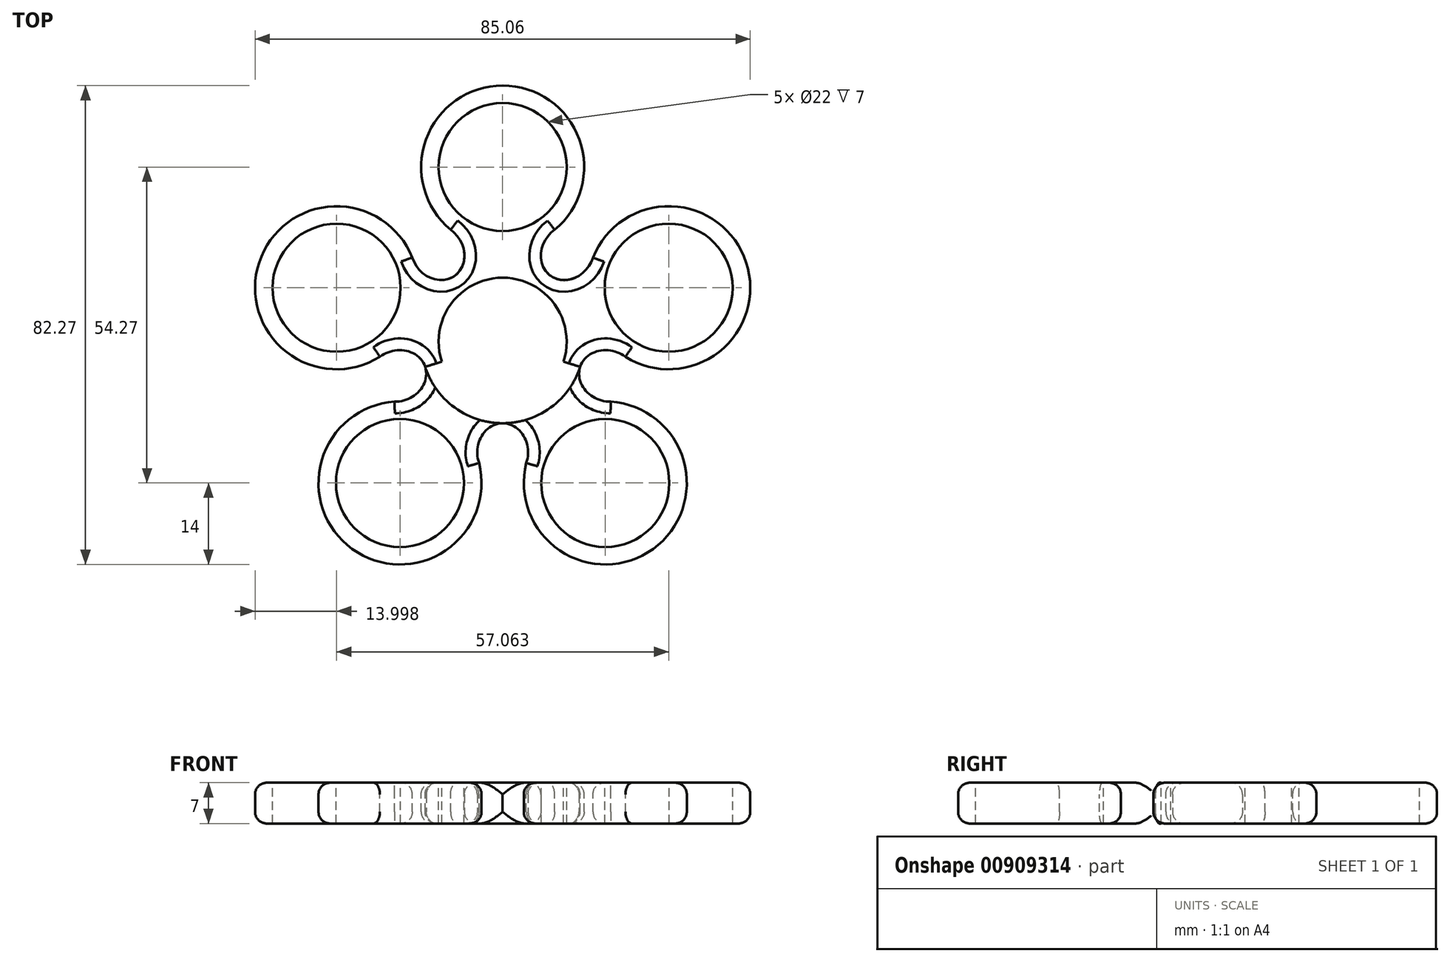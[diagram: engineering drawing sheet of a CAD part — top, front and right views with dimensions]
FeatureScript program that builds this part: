
annotation { "Feature Type Name" : "Feature", "Feature Type Description" : "" }
export const myFeature = defineFeature(function(context is Context, id is Id, definition is map)
    precondition{}
    {
        {
            var Q0;
            Q0=qCreatedBy(makeId("Top.planeOp"),FACE);
            var sketch = newSketch(context, id + "F0", { "sketchPlane" : qUnion([Q0])});
            skCircle(sketch, "E0", {"center": v(0, 0) * mm, "radius": 30 * mm});
            skCircle(sketch, "E1", {"center": v(0, 0) * mm, "radius": 44 * mm});
            skCircle(sketch, "E2.cCircle", {"center": v(0, 0) * mm, "radius": 44 * mm, "construction": true});
            skCircle(sketch, "E3.cCircle", {"center": v(0, 0) * mm, "radius": 30 * mm, "construction": true});
            skPoint(sketch, "E3.cCircle.perimeterSnap0", {"position": v(0, -19.5) * mm});
            skPoint(sketch, "E3.0.startSnap0", {"position": v(0, -24.5) * mm});
            skLineSegment(sketch, "E4", {"start": v(0, 44) * mm, "end": v(0, -30) * mm});
            skCircle(sketch, "E5", {"center": v(0, 30) * mm, "radius": 14 * mm});
            skCircle(sketch, "E6", {"center": v(0, 0) * mm, "radius": 11 * mm});
            skCircle(sketch, "E7", {"center": v(0, 30) * mm, "radius": 11 * mm});
            skPoint(sketch, "E8", {"position": v(29.84, 32.33) * mm});
            skLineSegment(sketch, "E9.0", {"start": v(0, 30) * mm, "end": v(28.53, 9.27) * mm});
            skLineSegment(sketch, "E9.1", {"start": v(28.53, 9.27) * mm, "end": v(17.63, -24.27) * mm});
            skLineSegment(sketch, "E9.2", {"start": v(17.63, -24.27) * mm, "end": v(-17.63, -24.27) * mm});
            skLineSegment(sketch, "E9.3", {"start": v(-17.63, -24.27) * mm, "end": v(-28.53, 9.27) * mm});
            skLineSegment(sketch, "E9.4", {"start": v(-28.53, 9.27) * mm, "end": v(0, 30) * mm});
            skCircle(sketch, "E10", {"center": v(28.53, 9.27) * mm, "radius": 14 * mm});
            skCircle(sketch, "E11", {"center": v(17.63, -24.27) * mm, "radius": 14 * mm});
            skCircle(sketch, "E12", {"center": v(-17.63, -24.27) * mm, "radius": 14 * mm});
            skCircle(sketch, "E13", {"center": v(-28.53, 9.27) * mm, "radius": 14 * mm});
            skCircle(sketch, "E14", {"center": v(-28.53, 9.27) * mm, "radius": 11 * mm});
            skCircle(sketch, "E15", {"center": v(-17.63, -24.27) * mm, "radius": 11 * mm});
            skCircle(sketch, "E16", {"center": v(17.63, -24.27) * mm, "radius": 11 * mm});
            skCircle(sketch, "E17", {"center": v(28.53, 9.27) * mm, "radius": 11 * mm});
            skCircle(sketch, "E18", {"center": v(0, 0) * mm, "radius": 14 * mm});
            skLineSegment(sketch, "E19", {"start": v(0, 0) * mm, "end": v(14.27, 19.64) * mm});
            skLineSegment(sketch, "E20", {"start": v(0, 0) * mm, "end": v(-14.27, 19.64) * mm});
            skLineSegment(sketch, "E21", {"start": v(0, 0) * mm, "end": v(-23.08, -7.5) * mm});
            skLineSegment(sketch, "E22", {"start": v(0, 0) * mm, "end": v(23.08, -7.5) * mm});
            skPoint(sketch, "E23", {"position": v(13.31, -4.33) * mm});
            skPoint(sketch, "E24", {"position": v(8.23, 11.33) * mm});
            skPoint(sketch, "E25", {"position": v(-8.23, 11.33) * mm});
            skPoint(sketch, "E26", {"position": v(-13.31, -4.33) * mm});
            skPoint(sketch, "E27", {"position": v(0, -14) * mm});
            skCircle(sketch, "E28", {"center": v(0, 0) * mm, "radius": 19 * mm});
            skEllipse(sketch, "E29", {"center": v(11.17, 15.37) * mm, "majorRadius": 5 * mm, "minorRadius": 4.36 * mm, "majorAxis": v(-0.59, -0.8)});
            skEllipse(sketch, "E30", {"center": v(-11.17, 15.37) * mm, "majorRadius": 5 * mm, "minorRadius": 4.36 * mm, "majorAxis": v(0.59, -0.8)});
            skEllipse(sketch, "E31", {"center": v(-18.07, -5.87) * mm, "majorRadius": 5 * mm, "minorRadius": 4.37 * mm, "majorAxis": v(0.95, 0.3)});
            skEllipse(sketch, "E32", {"center": v(0, -19) * mm, "majorRadius": 5 * mm, "minorRadius": 4.37 * mm, "majorAxis": v(0, 1)});
            skEllipse(sketch, "E33", {"center": v(18.07, -5.87) * mm, "majorRadius": 5 * mm, "minorRadius": 4.37 * mm, "majorAxis": v(-0.95, 0.3)});
            skSolve(sketch);
        }
        {
            var Q0;
            {var subQ0=sQuery(id+"F0.wireOp",EDGE,"rT3lhtyj-h4yS-NPWq-Tq2n-E2njMUcIvS19");var subQ1=sQuery(id+"F0.wireOp",EDGE,"E3.1");var subQ2=makeQuery(id+"F0.imprint","INTERSECT",VERTEX,{"derivedFrom":[subQ1,subQ0]});Q0=makeQuery(id+"F0.imprint","IMPRINT",FACE,{"disambiguationData":[TD([[makeQuery(id+"F0.imprint","IMPRINT",EDGE,{"disambiguationData":[TD([[subQ2,-1.0]])],"derivedFrom":subQ1}),1.0]])]});}
            var Q1;
            {var subQ0=sQuery(id+"F0.wireOp",EDGE,"E5");var subQ1=sQuery(id+"F0.wireOp",EDGE,"E3.1");var subQ2=makeQuery(id+"F0.imprint","INTERSECT",VERTEX,{"disambiguationData":[OD(1.0)],"derivedFrom":[subQ1,subQ0]});Q1=makeQuery(id+"F0.imprint","IMPRINT",FACE,{"disambiguationData":[TD([[makeQuery(id+"F0.imprint","IMPRINT",EDGE,{"disambiguationData":[TD([[subQ2,-1.0]])],"derivedFrom":subQ1}),1.0]])]});}
            var Q2;
            {var subQ0=sQuery(id+"F0.wireOp",EDGE,"E5");var subQ1=sQuery(id+"F0.wireOp",EDGE,"E0");var subQ2=makeQuery(id+"F0.imprint","INTERSECT",VERTEX,{"disambiguationData":[OD(0.0)],"derivedFrom":[subQ1,subQ0]});Q2=makeQuery(id+"F0.imprint","IMPRINT",FACE,{"disambiguationData":[TD([[makeQuery(id+"F0.imprint","IMPRINT",EDGE,{"disambiguationData":[TD([[subQ2,-1.0]])],"derivedFrom":subQ1}),-1.0]])]});}
            var Q3;
            {var subQ0=sQuery(id+"F0.wireOp",EDGE,"dxAisywA-VBGr-Pawd-wR7n-FkVNZc5FjTRd");var subQ1=sQuery(id+"F0.wireOp",EDGE,"E0");var subQ2=makeQuery(id+"F0.imprint","INTERSECT",VERTEX,{"disambiguationData":[OD(1.0)],"derivedFrom":[subQ1,subQ0]});Q3=makeQuery(id+"F0.imprint","IMPRINT",FACE,{"disambiguationData":[TD([[makeQuery(id+"F0.imprint","IMPRINT",EDGE,{"disambiguationData":[TD([[subQ2,-1.0]])],"derivedFrom":subQ1}),1.0]])]});}
            var Q4;
            {var subQ0=sQuery(id+"F0.wireOp",EDGE,"dxAisywA-VBGr-Pawd-wR7n-FkVNZc5FjTRd");var subQ1=sQuery(id+"F0.wireOp",EDGE,"E0");var subQ2=makeQuery(id+"F0.imprint","INTERSECT",VERTEX,{"disambiguationData":[OD(1.0)],"derivedFrom":[subQ1,subQ0]});Q4=makeQuery(id+"F0.imprint","IMPRINT",FACE,{"disambiguationData":[TD([[makeQuery(id+"F0.imprint","IMPRINT",EDGE,{"disambiguationData":[TD([[subQ2,-1.0]])],"derivedFrom":subQ1}),-1.0]])]});}
            var Q5;
            {var subQ0=sQuery(id+"F0.wireOp",EDGE,"dxAisywA-VBGr-Pawd-wR7n-FkVNZc5FjTRd");var subQ1=sQuery(id+"F0.wireOp",EDGE,"E0");var subQ2=makeQuery(id+"F0.imprint","INTERSECT",VERTEX,{"disambiguationData":[OD(0.0)],"derivedFrom":[subQ1,subQ0]});Q5=makeQuery(id+"F0.imprint","IMPRINT",FACE,{"disambiguationData":[TD([[makeQuery(id+"F0.imprint","IMPRINT",EDGE,{"disambiguationData":[TD([[subQ2,1.0]])],"derivedFrom":subQ1}),-1.0]])]});}
            var Q6;
            {var subQ0=sQuery(id+"F0.wireOp",EDGE,"RqG3pEgj-UPx2-bqY4-tycd-a4pZXK4rwrWL");var subQ1=sQuery(id+"F0.wireOp",EDGE,"E0");var subQ2=makeQuery(id+"F0.imprint","INTERSECT",VERTEX,{"disambiguationData":[OD(0.0)],"derivedFrom":[subQ1,subQ0]});Q6=makeQuery(id+"F0.imprint","IMPRINT",FACE,{"disambiguationData":[TD([[makeQuery(id+"F0.imprint","IMPRINT",EDGE,{"disambiguationData":[TD([[subQ2,-1.0]])],"derivedFrom":subQ1}),-1.0]])]});}
            var Q7;
            {var subQ0=sQuery(id+"F0.wireOp",EDGE,"RqG3pEgj-UPx2-bqY4-tycd-a4pZXK4rwrWL");var subQ1=sQuery(id+"F0.wireOp",EDGE,"E3.0");var subQ2=makeQuery(id+"F0.imprint","INTERSECT",VERTEX,{"disambiguationData":[OD(0.0)],"derivedFrom":[subQ1,subQ0]});Q7=makeQuery(id+"F0.imprint","IMPRINT",FACE,{"disambiguationData":[TD([[makeQuery(id+"F0.imprint","IMPRINT",EDGE,{"disambiguationData":[TD([[subQ2,-1.0]])],"derivedFrom":subQ1}),-1.0]])]});}
            var Q8;
            {var subQ0=sQuery(id+"F0.wireOp",EDGE,"0NMUeHQV-vgPk-UNAw-vjHk-L7wlCvfe4npe");var subQ1=sQuery(id+"F0.wireOp",EDGE,"E3.0");var subQ2=makeQuery(id+"F0.imprint","INTERSECT",VERTEX,{"derivedFrom":[subQ1,subQ0]});Q8=makeQuery(id+"F0.imprint","IMPRINT",FACE,{"disambiguationData":[TD([[makeQuery(id+"F0.imprint","IMPRINT",EDGE,{"disambiguationData":[TD([[subQ2,-1.0]])],"derivedFrom":subQ1}),-1.0]])]});}
            var Q9;
            {var subQ0=sQuery(id+"F0.wireOp",EDGE,"E5");var subQ1=sQuery(id+"F0.wireOp",EDGE,"E3.1");var subQ2=makeQuery(id+"F0.imprint","INTERSECT",VERTEX,{"disambiguationData":[OD(0.0)],"derivedFrom":[subQ1,subQ0]});Q9=makeQuery(id+"F0.imprint","IMPRINT",FACE,{"disambiguationData":[TD([[makeQuery(id+"F0.imprint","IMPRINT",EDGE,{"disambiguationData":[TD([[subQ2,-1.0]])],"derivedFrom":subQ1}),-1.0]])]});}
            var Q10;
            {var subQ0=sQuery(id+"F0.wireOp",EDGE,"dxAisywA-VBGr-Pawd-wR7n-FkVNZc5FjTRd");var subQ1=sQuery(id+"F0.wireOp",EDGE,"E3.2");var subQ2=makeQuery(id+"F0.imprint","INTERSECT",VERTEX,{"disambiguationData":[OD(0.0)],"derivedFrom":[subQ1,subQ0]});Q10=makeQuery(id+"F0.imprint","IMPRINT",FACE,{"disambiguationData":[TD([[makeQuery(id+"F0.imprint","IMPRINT",EDGE,{"disambiguationData":[TD([[subQ2,-1.0]])],"derivedFrom":subQ1}),-1.0]])]});}
            var Q11;
            {var subQ0=sQuery(id+"F0.wireOp",EDGE,"QKBKVQNg-VhWM-ZNxB-FvfL-6iABSSp7N5gX");var subQ1=sQuery(id+"F0.wireOp",EDGE,"E3.2");var subQ2=makeQuery(id+"F0.imprint","INTERSECT",VERTEX,{"derivedFrom":[subQ1,subQ0]});Q11=makeQuery(id+"F0.imprint","IMPRINT",FACE,{"disambiguationData":[TD([[makeQuery(id+"F0.imprint","IMPRINT",EDGE,{"disambiguationData":[TD([[subQ2,-1.0]])],"derivedFrom":subQ1}),-1.0]])]});}
            var Q12;
            {var subQ0=sQuery(id+"F0.wireOp",EDGE,"E5");var subQ1=sQuery(id+"F0.wireOp",EDGE,"E0");var subQ2=makeQuery(id+"F0.imprint","INTERSECT",VERTEX,{"disambiguationData":[OD(0.0)],"derivedFrom":[subQ1,subQ0]});Q12=makeQuery(id+"F0.imprint","IMPRINT",FACE,{"disambiguationData":[TD([[makeQuery(id+"F0.imprint","IMPRINT",EDGE,{"disambiguationData":[TD([[subQ2,-1.0]])],"derivedFrom":subQ1}),1.0]])]});}
            var Q13;
            {var subQ0=sQuery(id+"F0.wireOp",EDGE,"dxAisywA-VBGr-Pawd-wR7n-FkVNZc5FjTRd");var subQ1=sQuery(id+"F0.wireOp",EDGE,"E0");var subQ2=makeQuery(id+"F0.imprint","INTERSECT",VERTEX,{"disambiguationData":[OD(0.0)],"derivedFrom":[subQ1,subQ0]});Q13=makeQuery(id+"F0.imprint","IMPRINT",FACE,{"disambiguationData":[TD([[makeQuery(id+"F0.imprint","IMPRINT",EDGE,{"disambiguationData":[TD([[subQ2,1.0]])],"derivedFrom":subQ1}),1.0]])]});}
            var Q14;
            {var subQ0=sQuery(id+"F0.wireOp",EDGE,"RqG3pEgj-UPx2-bqY4-tycd-a4pZXK4rwrWL");var subQ1=sQuery(id+"F0.wireOp",EDGE,"E0");var subQ2=makeQuery(id+"F0.imprint","INTERSECT",VERTEX,{"disambiguationData":[OD(0.0)],"derivedFrom":[subQ1,subQ0]});Q14=makeQuery(id+"F0.imprint","IMPRINT",FACE,{"disambiguationData":[TD([[makeQuery(id+"F0.imprint","IMPRINT",EDGE,{"disambiguationData":[TD([[subQ2,-1.0]])],"derivedFrom":subQ1}),1.0]])]});}
            var Q15;
            {var subQ0=sQuery(id+"F0.wireOp",EDGE,"E4");var subQ1=sQuery(id+"F0.wireOp",EDGE,"E3.1");var subQ2=makeQuery(id+"F0.imprint","INTERSECT",VERTEX,{"derivedFrom":[subQ1,subQ0]});Q15=makeQuery(id+"F0.imprint","IMPRINT",FACE,{"disambiguationData":[TD([[makeQuery(id+"F0.imprint","IMPRINT",EDGE,{"disambiguationData":[TD([[subQ2,-1.0]])],"derivedFrom":subQ1}),-1.0]])]});}
            var Q16;
            {var subQ1=sQuery(id+"F0.wireOp",EDGE,"E3.1");var subQ5=sQuery(id+"F0.wireOp",EDGE,"E5");var subQ6=makeQuery(id+"F0.imprint","INTERSECT",VERTEX,{"disambiguationData":[OD(1.0)],"derivedFrom":[subQ1,subQ5]});Q16=makeQuery(id+"F0.imprint","IMPRINT",FACE,{"disambiguationData":[TD([[makeQuery(id+"F0.imprint","IMPRINT",EDGE,{"disambiguationData":[TD([[subQ6,-1.0]])],"derivedFrom":subQ1}),-1.0]])]});}
            var Q17;
            {var subQ1=sQuery(id+"F0.wireOp",EDGE,"E3.2");var subQ5=sQuery(id+"F0.wireOp",EDGE,"sHA2WUK1-COiN-vLBo-81U8-SncWV65uhgPs");var subQ9=makeQuery(id+"F0.imprint","INTERSECT",VERTEX,{"derivedFrom":[subQ1,subQ5]});Q17=makeQuery(id+"F0.imprint","IMPRINT",FACE,{"disambiguationData":[TD([[makeQuery(id+"F0.imprint","IMPRINT",EDGE,{"disambiguationData":[TD([[subQ9,-1.0]])],"derivedFrom":subQ1}),-1.0]])]});}
            var Q18;
            {var subQ1=sQuery(id+"F0.wireOp",EDGE,"E3.0");var subQ5=sQuery(id+"F0.wireOp",EDGE,"RqG3pEgj-UPx2-bqY4-tycd-a4pZXK4rwrWL");var subQ6=makeQuery(id+"F0.imprint","INTERSECT",VERTEX,{"disambiguationData":[OD(1.0)],"derivedFrom":[subQ1,subQ5]});Q18=makeQuery(id+"F0.imprint","IMPRINT",FACE,{"disambiguationData":[TD([[makeQuery(id+"F0.imprint","IMPRINT",EDGE,{"disambiguationData":[TD([[subQ6,-1.0]])],"derivedFrom":subQ1}),-1.0]])]});}
            var Q19;
            {var subQ1=sQuery(id+"F0.wireOp",EDGE,"E3.0");var subQ7=sQuery(id+"F0.wireOp",EDGE,"ZJlmTgZx-EINA-FnJ0-EF4e-C9FzmJizpjkO");var subQ9=makeQuery(id+"F0.imprint","INTERSECT",VERTEX,{"derivedFrom":[subQ1,subQ7]});Q19=makeQuery(id+"F0.imprint","IMPRINT",FACE,{"disambiguationData":[TD([[makeQuery(id+"F0.imprint","IMPRINT",EDGE,{"disambiguationData":[TD([[subQ9,-1.0]])],"derivedFrom":subQ1}),-1.0]])]});}
            var Q20;
            {var subQ1=sQuery(id+"F0.wireOp",EDGE,"E3.2");var subQ7=sQuery(id+"F0.wireOp",EDGE,"dxAisywA-VBGr-Pawd-wR7n-FkVNZc5FjTRd");var subQ8=makeQuery(id+"F0.imprint","INTERSECT",VERTEX,{"disambiguationData":[OD(1.0)],"derivedFrom":[subQ1,subQ7]});Q20=makeQuery(id+"F0.imprint","IMPRINT",FACE,{"disambiguationData":[TD([[makeQuery(id+"F0.imprint","IMPRINT",EDGE,{"disambiguationData":[TD([[subQ8,-1.0]])],"derivedFrom":subQ1}),-1.0]])]});}
            var Q21;
            {var subQ0=sQuery(id+"F0.wireOp",EDGE,"RqG3pEgj-UPx2-bqY4-tycd-a4pZXK4rwrWL");var subQ1=sQuery(id+"F0.wireOp",EDGE,"E3.0");var subQ2=makeQuery(id+"F0.imprint","INTERSECT",VERTEX,{"disambiguationData":[OD(1.0)],"derivedFrom":[subQ1,subQ0]});Q21=makeQuery(id+"F0.imprint","IMPRINT",FACE,{"disambiguationData":[TD([[makeQuery(id+"F0.imprint","IMPRINT",EDGE,{"disambiguationData":[TD([[subQ2,-1.0]])],"derivedFrom":subQ1}),1.0]])]});}
            var Q22;
            {var subQ0=sQuery(id+"F0.wireOp",EDGE,"sHA2WUK1-COiN-vLBo-81U8-SncWV65uhgPs");var subQ1=sQuery(id+"F0.wireOp",EDGE,"E3.2");var subQ2=makeQuery(id+"F0.imprint","INTERSECT",VERTEX,{"derivedFrom":[subQ1,subQ0]});Q22=makeQuery(id+"F0.imprint","IMPRINT",FACE,{"disambiguationData":[TD([[makeQuery(id+"F0.imprint","IMPRINT",EDGE,{"disambiguationData":[TD([[subQ2,-1.0]])],"derivedFrom":subQ1}),1.0]])]});}
            var Q23;
            {var subQ0=sQuery(id+"F0.wireOp",EDGE,"ZJlmTgZx-EINA-FnJ0-EF4e-C9FzmJizpjkO");var subQ1=sQuery(id+"F0.wireOp",EDGE,"E3.0");var subQ2=makeQuery(id+"F0.imprint","INTERSECT",VERTEX,{"derivedFrom":[subQ1,subQ0]});Q23=makeQuery(id+"F0.imprint","IMPRINT",FACE,{"disambiguationData":[TD([[makeQuery(id+"F0.imprint","IMPRINT",EDGE,{"disambiguationData":[TD([[subQ2,-1.0]])],"derivedFrom":subQ1}),1.0]])]});}
            var Q24;
            {var subQ0=sQuery(id+"F0.wireOp",EDGE,"dxAisywA-VBGr-Pawd-wR7n-FkVNZc5FjTRd");var subQ1=sQuery(id+"F0.wireOp",EDGE,"E3.2");var subQ2=makeQuery(id+"F0.imprint","INTERSECT",VERTEX,{"disambiguationData":[OD(1.0)],"derivedFrom":[subQ1,subQ0]});Q24=makeQuery(id+"F0.imprint","IMPRINT",FACE,{"disambiguationData":[TD([[makeQuery(id+"F0.imprint","IMPRINT",EDGE,{"disambiguationData":[TD([[subQ2,-1.0]])],"derivedFrom":subQ1}),1.0]])]});}
            var Q25;
            {var subQ0=sQuery(id+"F0.wireOp",EDGE,"rT3lhtyj-h4yS-NPWq-Tq2n-E2njMUcIvS19");var subQ1=sQuery(id+"F0.wireOp",EDGE,"E3.1");var subQ2=makeQuery(id+"F0.imprint","INTERSECT",VERTEX,{"derivedFrom":[subQ1,subQ0]});Q25=makeQuery(id+"F0.imprint","IMPRINT",FACE,{"disambiguationData":[TD([[makeQuery(id+"F0.imprint","IMPRINT",EDGE,{"disambiguationData":[TD([[subQ2,-1.0]])],"derivedFrom":subQ1}),-1.0]])]});}
            var Q26;
            {var subQ1=sQuery(id+"F0.wireOp",EDGE,"E2.1");var subQ3=sQuery(id+"F0.wireOp",EDGE,"pn2p9FIU-HhLt-bJUs-He3U-jyiwcetz7rk5");var subQ4=makeQuery(id+"F0.imprint","INTERSECT",VERTEX,{"disambiguationData":[OD(1.0)],"derivedFrom":[subQ1,subQ3]});Q26=makeQuery(id+"F0.imprint","IMPRINT",FACE,{"disambiguationData":[TD([[makeQuery(id+"F0.imprint","IMPRINT",EDGE,{"disambiguationData":[TD([[subQ4,1.0]])],"derivedFrom":subQ3}),-1.0]])]});}
            var Q27;
            {var subQ0=sQuery(id+"F0.wireOp",EDGE,"pn2p9FIU-HhLt-bJUs-He3U-jyiwcetz7rk5");var subQ1=sQuery(id+"F0.wireOp",EDGE,"E0");var subQ2=makeQuery(id+"F0.imprint","INTERSECT",VERTEX,{"disambiguationData":[OD(1.0)],"derivedFrom":[subQ1,subQ0]});Q27=makeQuery(id+"F0.imprint","IMPRINT",FACE,{"disambiguationData":[TD([[makeQuery(id+"F0.imprint","IMPRINT",EDGE,{"disambiguationData":[TD([[subQ2,-1.0]])],"derivedFrom":subQ1}),-1.0]])]});}
            var Q28;
            {var subQ0=sQuery(id+"F0.wireOp",EDGE,"pn2p9FIU-HhLt-bJUs-He3U-jyiwcetz7rk5");var subQ1=sQuery(id+"F0.wireOp",EDGE,"E0");var subQ2=makeQuery(id+"F0.imprint","INTERSECT",VERTEX,{"disambiguationData":[OD(1.0)],"derivedFrom":[subQ1,subQ0]});Q28=makeQuery(id+"F0.imprint","IMPRINT",FACE,{"disambiguationData":[TD([[makeQuery(id+"F0.imprint","IMPRINT",EDGE,{"disambiguationData":[TD([[subQ2,-1.0]])],"derivedFrom":subQ1}),1.0]])]});}
            var Q29;
            {var subQ0=sQuery(id+"F0.wireOp",EDGE,"RqG3pEgj-UPx2-bqY4-tycd-a4pZXK4rwrWL");var subQ1=sQuery(id+"F0.wireOp",EDGE,"E3.0");var subQ2=makeQuery(id+"F0.imprint","INTERSECT",VERTEX,{"disambiguationData":[OD(0.0)],"derivedFrom":[subQ1,subQ0]});Q29=makeQuery(id+"F0.imprint","IMPRINT",FACE,{"disambiguationData":[TD([[makeQuery(id+"F0.imprint","IMPRINT",EDGE,{"disambiguationData":[TD([[subQ2,-1.0]])],"derivedFrom":subQ1}),1.0]])]});}
            var Q30;
            {var subQ1=sQuery(id+"F0.wireOp",EDGE,"E2.2");var subQ3=sQuery(id+"F0.wireOp",EDGE,"pn2p9FIU-HhLt-bJUs-He3U-jyiwcetz7rk5");var subQ4=makeQuery(id+"F0.imprint","INTERSECT",VERTEX,{"disambiguationData":[OD(0.0)],"derivedFrom":[subQ1,subQ3]});Q30=makeQuery(id+"F0.imprint","IMPRINT",FACE,{"disambiguationData":[TD([[makeQuery(id+"F0.imprint","IMPRINT",EDGE,{"disambiguationData":[TD([[subQ4,-1.0]])],"derivedFrom":subQ3}),-1.0]])]});}
            var Q31;
            {var subQ1=sQuery(id+"F0.wireOp",EDGE,"E3.0");var subQ5=sQuery(id+"F0.wireOp",EDGE,"0NMUeHQV-vgPk-UNAw-vjHk-L7wlCvfe4npe");var subQ6=makeQuery(id+"F0.imprint","INTERSECT",VERTEX,{"derivedFrom":[subQ1,subQ5]});Q31=makeQuery(id+"F0.imprint","IMPRINT",FACE,{"disambiguationData":[TD([[makeQuery(id+"F0.imprint","IMPRINT",EDGE,{"disambiguationData":[TD([[subQ6,-1.0]])],"derivedFrom":subQ1}),1.0]])]});}
            var Q32;
            {var subQ1=sQuery(id+"F0.wireOp",EDGE,"E3.2");var subQ5=sQuery(id+"F0.wireOp",EDGE,"QKBKVQNg-VhWM-ZNxB-FvfL-6iABSSp7N5gX");var subQ6=makeQuery(id+"F0.imprint","INTERSECT",VERTEX,{"derivedFrom":[subQ1,subQ5]});Q32=makeQuery(id+"F0.imprint","IMPRINT",FACE,{"disambiguationData":[TD([[makeQuery(id+"F0.imprint","IMPRINT",EDGE,{"disambiguationData":[TD([[subQ6,-1.0]])],"derivedFrom":subQ1}),1.0]])]});}
            var Q33;
            {var subQ1=sQuery(id+"F0.wireOp",EDGE,"E3.2");var subQ7=sQuery(id+"F0.wireOp",EDGE,"dxAisywA-VBGr-Pawd-wR7n-FkVNZc5FjTRd");var subQ9=makeQuery(id+"F0.imprint","INTERSECT",VERTEX,{"disambiguationData":[OD(0.0)],"derivedFrom":[subQ1,subQ7]});Q33=makeQuery(id+"F0.imprint","IMPRINT",FACE,{"disambiguationData":[TD([[makeQuery(id+"F0.imprint","IMPRINT",EDGE,{"disambiguationData":[TD([[subQ9,-1.0]])],"derivedFrom":subQ1}),1.0]])]});}
            var Q34;
            {var subQ1=sQuery(id+"F0.wireOp",EDGE,"E2.1");var subQ3=sQuery(id+"F0.wireOp",EDGE,"wBWbJlWF-WJeb-dRll-Lu5Z-CJGq9FSQDJmP");var subQ4=makeQuery(id+"F0.imprint","INTERSECT",VERTEX,{"disambiguationData":[OD(0.0)],"derivedFrom":[subQ1,subQ3]});Q34=makeQuery(id+"F0.imprint","IMPRINT",FACE,{"disambiguationData":[TD([[makeQuery(id+"F0.imprint","IMPRINT",EDGE,{"disambiguationData":[TD([[subQ4,-1.0]])],"derivedFrom":subQ3}),-1.0]])]});}
            var Q35;
            {var subQ1=sQuery(id+"F0.wireOp",EDGE,"E2.0");var subQ3=sQuery(id+"F0.wireOp",EDGE,"wBWbJlWF-WJeb-dRll-Lu5Z-CJGq9FSQDJmP");var subQ4=makeQuery(id+"F0.imprint","INTERSECT",VERTEX,{"disambiguationData":[OD(1.0)],"derivedFrom":[subQ1,subQ3]});Q35=makeQuery(id+"F0.imprint","IMPRINT",FACE,{"disambiguationData":[TD([[makeQuery(id+"F0.imprint","IMPRINT",EDGE,{"disambiguationData":[TD([[subQ4,1.0]])],"derivedFrom":subQ3}),-1.0]])]});}
            var Q36;
            {var subQ1=sQuery(id+"F0.wireOp",EDGE,"E3.1");var subQ5=sQuery(id+"F0.wireOp",EDGE,"E4");var subQ6=makeQuery(id+"F0.imprint","INTERSECT",VERTEX,{"derivedFrom":[subQ1,subQ5]});Q36=makeQuery(id+"F0.imprint","IMPRINT",FACE,{"disambiguationData":[TD([[makeQuery(id+"F0.imprint","IMPRINT",EDGE,{"disambiguationData":[TD([[subQ6,-1.0]])],"derivedFrom":subQ1}),1.0]])]});}
            var Q37;
            {var subQ1=sQuery(id+"F0.wireOp",EDGE,"E3.1");var subQ5=sQuery(id+"F0.wireOp",EDGE,"E5");var subQ6=makeQuery(id+"F0.imprint","INTERSECT",VERTEX,{"disambiguationData":[OD(0.0)],"derivedFrom":[subQ1,subQ5]});Q37=makeQuery(id+"F0.imprint","IMPRINT",FACE,{"disambiguationData":[TD([[makeQuery(id+"F0.imprint","IMPRINT",EDGE,{"disambiguationData":[TD([[subQ6,-1.0]])],"derivedFrom":subQ1}),1.0]])]});}
            var Q38;
            {var subQ0=sQuery(id+"F0.wireOp",EDGE,"E7");var subQ1=sQuery(id+"F0.wireOp",EDGE,"E0");var subQ2=makeQuery(id+"F0.imprint","INTERSECT",VERTEX,{"disambiguationData":[OD(1.0)],"derivedFrom":[subQ1,subQ0]});Q38=makeQuery(id+"F0.imprint","IMPRINT",FACE,{"disambiguationData":[TD([[makeQuery(id+"F0.imprint","IMPRINT",EDGE,{"disambiguationData":[TD([[subQ2,-1.0]])],"derivedFrom":subQ1}),-1.0]])]});}
            var Q39;
            {var subQ0=sQuery(id+"F0.wireOp",EDGE,"E7");var subQ1=sQuery(id+"F0.wireOp",EDGE,"E0");var subQ2=makeQuery(id+"F0.imprint","INTERSECT",VERTEX,{"disambiguationData":[OD(1.0)],"derivedFrom":[subQ1,subQ0]});Q39=makeQuery(id+"F0.imprint","IMPRINT",FACE,{"disambiguationData":[TD([[makeQuery(id+"F0.imprint","IMPRINT",EDGE,{"disambiguationData":[TD([[subQ2,-1.0]])],"derivedFrom":subQ1}),1.0]])]});}
            var Q40;
            {var subQ1=sQuery(id+"F0.wireOp",EDGE,"E2.0");var subQ3=sQuery(id+"F0.wireOp",EDGE,"E7");var subQ4=makeQuery(id+"F0.imprint","INTERSECT",VERTEX,{"disambiguationData":[OD(0.0)],"derivedFrom":[subQ1,subQ3]});Q40=makeQuery(id+"F0.imprint","IMPRINT",FACE,{"disambiguationData":[TD([[makeQuery(id+"F0.imprint","IMPRINT",EDGE,{"disambiguationData":[TD([[subQ4,-1.0]])],"derivedFrom":subQ3}),-1.0]])]});}
            var Q41;
            {var subQ1=sQuery(id+"F0.wireOp",EDGE,"E2.2");var subQ3=sQuery(id+"F0.wireOp",EDGE,"E7");var subQ4=makeQuery(id+"F0.imprint","INTERSECT",VERTEX,{"disambiguationData":[OD(1.0)],"derivedFrom":[subQ1,subQ3]});Q41=makeQuery(id+"F0.imprint","IMPRINT",FACE,{"disambiguationData":[TD([[makeQuery(id+"F0.imprint","IMPRINT",EDGE,{"disambiguationData":[TD([[subQ4,1.0]])],"derivedFrom":subQ3}),-1.0]])]});}
            var Q42;
            {var subQ1=sQuery(id+"F0.wireOp",EDGE,"E5");var subQ8=sQuery(id+"F0.wireOp",EDGE,"E28");var subQ10=makeQuery(id+"F0.imprint","INTERSECT",VERTEX,{"disambiguationData":[OD(1.0)],"derivedFrom":[subQ1,subQ8]});Q42=makeQuery(id+"F0.imprint","IMPRINT",FACE,{"disambiguationData":[TD([[makeQuery(id+"F0.imprint","IMPRINT",EDGE,{"disambiguationData":[TD([[subQ10,-1.0]])],"derivedFrom":subQ1}),1.0]])]});}
            var Q43;
            {var subQ0=sQuery(id+"F0.wireOp",EDGE,"E5");var subQ1=sQuery(id+"F0.wireOp",EDGE,"E4");var subQ2=makeQuery(id+"F0.imprint","INTERSECT",VERTEX,{"derivedFrom":[subQ1,subQ0]});Q43=makeQuery(id+"F0.imprint","IMPRINT",FACE,{"disambiguationData":[TD([[makeQuery(id+"F0.imprint","IMPRINT",EDGE,{"disambiguationData":[TD([[subQ2,-1.0]])],"derivedFrom":subQ0}),1.0]])]});}
            var Q44;
            {var subQ0=sQuery(id+"F0.wireOp",EDGE,"E5");var subQ1=sQuery(id+"F0.wireOp",EDGE,"E4");var subQ2=makeQuery(id+"F0.imprint","INTERSECT",VERTEX,{"derivedFrom":[subQ1,subQ0]});Q44=makeQuery(id+"F0.imprint","IMPRINT",FACE,{"disambiguationData":[TD([[makeQuery(id+"F0.imprint","IMPRINT",EDGE,{"disambiguationData":[TD([[subQ2,1.0]])],"derivedFrom":subQ0}),1.0]])]});}
            var Q45;
            {var subQ0=sQuery(id+"F0.wireOp",EDGE,"E9.4");var subQ6=sQuery(id+"F0.wireOp",EDGE,"E5");var subQ9=makeQuery(id+"F0.imprint","INTERSECT",VERTEX,{"derivedFrom":[subQ6,subQ0]});Q45=makeQuery(id+"F0.imprint","IMPRINT",FACE,{"disambiguationData":[TD([[makeQuery(id+"F0.imprint","IMPRINT",EDGE,{"disambiguationData":[TD([[subQ9,-1.0]])],"derivedFrom":subQ6}),1.0]])]});}
            var Q46;
            {var subQ2=sQuery(id+"F0.wireOp",EDGE,"E0");var subQ5=sQuery(id+"F0.wireOp",EDGE,"E17");var subQ7=makeQuery(id+"F0.imprint","INTERSECT",VERTEX,{"disambiguationData":[OD(0.0)],"derivedFrom":[subQ2,subQ5]});Q46=makeQuery(id+"F0.imprint","IMPRINT",FACE,{"disambiguationData":[TD([[makeQuery(id+"F0.imprint","IMPRINT",EDGE,{"disambiguationData":[TD([[subQ7,-1.0]])],"derivedFrom":subQ2}),-1.0]])]});}
            var Q47;
            {var subQ0=sQuery(id+"F0.wireOp",EDGE,"E17");var subQ1=sQuery(id+"F0.wireOp",EDGE,"E0");var subQ2=makeQuery(id+"F0.imprint","INTERSECT",VERTEX,{"disambiguationData":[OD(0.0)],"derivedFrom":[subQ1,subQ0]});Q47=makeQuery(id+"F0.imprint","IMPRINT",FACE,{"disambiguationData":[TD([[makeQuery(id+"F0.imprint","IMPRINT",EDGE,{"disambiguationData":[TD([[subQ2,-1.0]])],"derivedFrom":subQ1}),1.0]])]});}
            var Q48;
            {var subQ1=sQuery(id+"F0.wireOp",EDGE,"E9.0");var subQ5=sQuery(id+"F0.wireOp",EDGE,"E10");var subQ6=makeQuery(id+"F0.imprint","INTERSECT",VERTEX,{"derivedFrom":[subQ1,subQ5]});Q48=makeQuery(id+"F0.imprint","IMPRINT",FACE,{"disambiguationData":[TD([[makeQuery(id+"F0.imprint","IMPRINT",EDGE,{"disambiguationData":[TD([[subQ6,-1.0]])],"derivedFrom":subQ1}),-1.0]])]});}
            var Q49;
            {var subQ0=sQuery(id+"F0.wireOp",EDGE,"E28");var subQ1=sQuery(id+"F0.wireOp",EDGE,"E10");var subQ2=makeQuery(id+"F0.imprint","INTERSECT",VERTEX,{"disambiguationData":[OD(0.0)],"derivedFrom":[subQ1,subQ0]});Q49=makeQuery(id+"F0.imprint","IMPRINT",FACE,{"disambiguationData":[TD([[makeQuery(id+"F0.imprint","IMPRINT",EDGE,{"disambiguationData":[TD([[subQ2,-1.0]])],"derivedFrom":subQ1}),1.0]])]});}
            var Q50;
            {var subQ1=sQuery(id+"F0.wireOp",EDGE,"E9.1");var subQ5=sQuery(id+"F0.wireOp",EDGE,"E17");var subQ6=makeQuery(id+"F0.imprint","INTERSECT",VERTEX,{"derivedFrom":[subQ1,subQ5]});Q50=makeQuery(id+"F0.imprint","IMPRINT",FACE,{"disambiguationData":[TD([[makeQuery(id+"F0.imprint","IMPRINT",EDGE,{"disambiguationData":[TD([[subQ6,-1.0]])],"derivedFrom":subQ1}),-1.0]])]});}
            var Q51;
            {var subQ0=sQuery(id+"F0.wireOp",EDGE,"E10");var subQ1=sQuery(id+"F0.wireOp",EDGE,"E0");var subQ2=makeQuery(id+"F0.imprint","INTERSECT",VERTEX,{"disambiguationData":[OD(1.0)],"derivedFrom":[subQ1,subQ0]});Q51=makeQuery(id+"F0.imprint","IMPRINT",FACE,{"disambiguationData":[TD([[makeQuery(id+"F0.imprint","IMPRINT",EDGE,{"disambiguationData":[TD([[subQ2,-1.0]])],"derivedFrom":subQ1}),1.0]])]});}
            var Q52;
            {var subQ0=sQuery(id+"F0.wireOp",EDGE,"E11");var subQ2=sQuery(id+"F0.wireOp",EDGE,"E0");var subQ3=makeQuery(id+"F0.imprint","INTERSECT",VERTEX,{"disambiguationData":[OD(0.0)],"derivedFrom":[subQ2,subQ0]});Q52=makeQuery(id+"F0.imprint","IMPRINT",FACE,{"disambiguationData":[TD([[makeQuery(id+"F0.imprint","IMPRINT",EDGE,{"disambiguationData":[TD([[subQ3,-1.0]])],"derivedFrom":subQ2}),-1.0]])]});}
            var Q53;
            {var subQ0=sQuery(id+"F0.wireOp",EDGE,"E16");var subQ1=sQuery(id+"F0.wireOp",EDGE,"E0");var subQ2=makeQuery(id+"F0.imprint","INTERSECT",VERTEX,{"disambiguationData":[OD(1.0)],"derivedFrom":[subQ1,subQ0]});Q53=makeQuery(id+"F0.imprint","IMPRINT",FACE,{"disambiguationData":[TD([[makeQuery(id+"F0.imprint","IMPRINT",EDGE,{"disambiguationData":[TD([[subQ2,-1.0]])],"derivedFrom":subQ1}),1.0]])]});}
            var Q54;
            {var subQ0=sQuery(id+"F0.wireOp",EDGE,"E11");var subQ1=sQuery(id+"F0.wireOp",EDGE,"E0");var subQ2=makeQuery(id+"F0.imprint","INTERSECT",VERTEX,{"disambiguationData":[OD(0.0)],"derivedFrom":[subQ1,subQ0]});Q54=makeQuery(id+"F0.imprint","IMPRINT",FACE,{"disambiguationData":[TD([[makeQuery(id+"F0.imprint","IMPRINT",EDGE,{"disambiguationData":[TD([[subQ2,-1.0]])],"derivedFrom":subQ1}),1.0]])]});}
            var Q55;
            {var subQ0=sQuery(id+"F0.wireOp",EDGE,"E16");var subQ1=sQuery(id+"F0.wireOp",EDGE,"E9.2");var subQ2=makeQuery(id+"F0.imprint","INTERSECT",VERTEX,{"derivedFrom":[subQ1,subQ0]});Q55=makeQuery(id+"F0.imprint","IMPRINT",FACE,{"disambiguationData":[TD([[makeQuery(id+"F0.imprint","IMPRINT",EDGE,{"disambiguationData":[TD([[subQ2,-1.0]])],"derivedFrom":subQ1}),-1.0]])]});}
            var Q56;
            {var subQ0=sQuery(id+"F0.wireOp",EDGE,"E28");var subQ1=sQuery(id+"F0.wireOp",EDGE,"E11");var subQ2=makeQuery(id+"F0.imprint","INTERSECT",VERTEX,{"disambiguationData":[OD(0.0)],"derivedFrom":[subQ1,subQ0]});Q56=makeQuery(id+"F0.imprint","IMPRINT",FACE,{"disambiguationData":[TD([[makeQuery(id+"F0.imprint","IMPRINT",EDGE,{"disambiguationData":[TD([[subQ2,-1.0]])],"derivedFrom":subQ1}),1.0]])]});}
            var Q57;
            {var subQ1=sQuery(id+"F0.wireOp",EDGE,"E11");var subQ5=sQuery(id+"F0.wireOp",EDGE,"E9.1");var subQ6=makeQuery(id+"F0.imprint","INTERSECT",VERTEX,{"derivedFrom":[subQ5,subQ1]});Q57=makeQuery(id+"F0.imprint","IMPRINT",FACE,{"disambiguationData":[TD([[makeQuery(id+"F0.imprint","IMPRINT",EDGE,{"disambiguationData":[TD([[subQ6,-1.0]])],"derivedFrom":subQ5}),-1.0]])]});}
            var Q58;
            {var subQ1=sQuery(id+"F0.wireOp",EDGE,"E9.2");var subQ6=sQuery(id+"F0.wireOp",EDGE,"E12");var subQ9=makeQuery(id+"F0.imprint","INTERSECT",VERTEX,{"derivedFrom":[subQ1,subQ6]});Q58=makeQuery(id+"F0.imprint","IMPRINT",FACE,{"disambiguationData":[TD([[makeQuery(id+"F0.imprint","IMPRINT",EDGE,{"disambiguationData":[TD([[subQ9,-1.0]])],"derivedFrom":subQ1}),-1.0]])]});}
            var Q59;
            {var subQ0=sQuery(id+"F0.wireOp",EDGE,"E15");var subQ1=sQuery(id+"F0.wireOp",EDGE,"E0");var subQ2=makeQuery(id+"F0.imprint","INTERSECT",VERTEX,{"disambiguationData":[OD(1.0)],"derivedFrom":[subQ1,subQ0]});Q59=makeQuery(id+"F0.imprint","IMPRINT",FACE,{"disambiguationData":[TD([[makeQuery(id+"F0.imprint","IMPRINT",EDGE,{"disambiguationData":[TD([[subQ2,-1.0]])],"derivedFrom":subQ1}),1.0]])]});}
            var Q60;
            {var subQ0=sQuery(id+"F0.wireOp",EDGE,"E12");var subQ2=sQuery(id+"F0.wireOp",EDGE,"E0");var subQ6=makeQuery(id+"F0.imprint","INTERSECT",VERTEX,{"disambiguationData":[OD(0.0)],"derivedFrom":[subQ2,subQ0]});Q60=makeQuery(id+"F0.imprint","IMPRINT",FACE,{"disambiguationData":[TD([[makeQuery(id+"F0.imprint","IMPRINT",EDGE,{"disambiguationData":[TD([[subQ6,-1.0]])],"derivedFrom":subQ2}),-1.0]])]});}
            var Q61;
            {var subQ0=sQuery(id+"F0.wireOp",EDGE,"E12");var subQ1=sQuery(id+"F0.wireOp",EDGE,"E0");var subQ2=makeQuery(id+"F0.imprint","INTERSECT",VERTEX,{"disambiguationData":[OD(0.0)],"derivedFrom":[subQ1,subQ0]});Q61=makeQuery(id+"F0.imprint","IMPRINT",FACE,{"disambiguationData":[TD([[makeQuery(id+"F0.imprint","IMPRINT",EDGE,{"disambiguationData":[TD([[subQ2,-1.0]])],"derivedFrom":subQ1}),1.0]])]});}
            var Q62;
            {var subQ0=sQuery(id+"F0.wireOp",EDGE,"E15");var subQ1=sQuery(id+"F0.wireOp",EDGE,"E9.3");var subQ2=makeQuery(id+"F0.imprint","INTERSECT",VERTEX,{"derivedFrom":[subQ1,subQ0]});Q62=makeQuery(id+"F0.imprint","IMPRINT",FACE,{"disambiguationData":[TD([[makeQuery(id+"F0.imprint","IMPRINT",EDGE,{"disambiguationData":[TD([[subQ2,-1.0]])],"derivedFrom":subQ1}),-1.0]])]});}
            var Q63;
            {var subQ0=sQuery(id+"F0.wireOp",EDGE,"E28");var subQ1=sQuery(id+"F0.wireOp",EDGE,"E12");var subQ2=makeQuery(id+"F0.imprint","INTERSECT",VERTEX,{"disambiguationData":[OD(0.0)],"derivedFrom":[subQ1,subQ0]});Q63=makeQuery(id+"F0.imprint","IMPRINT",FACE,{"disambiguationData":[TD([[makeQuery(id+"F0.imprint","IMPRINT",EDGE,{"disambiguationData":[TD([[subQ2,-1.0]])],"derivedFrom":subQ1}),1.0]])]});}
            var Q64;
            {var subQ0=sQuery(id+"F0.wireOp",EDGE,"E13");var subQ2=sQuery(id+"F0.wireOp",EDGE,"E0");var subQ3=makeQuery(id+"F0.imprint","INTERSECT",VERTEX,{"disambiguationData":[OD(0.0)],"derivedFrom":[subQ2,subQ0]});Q64=makeQuery(id+"F0.imprint","IMPRINT",FACE,{"disambiguationData":[TD([[makeQuery(id+"F0.imprint","IMPRINT",EDGE,{"disambiguationData":[TD([[subQ3,-1.0]])],"derivedFrom":subQ2}),-1.0]])]});}
            var Q65;
            {var subQ0=sQuery(id+"F0.wireOp",EDGE,"E14");var subQ1=sQuery(id+"F0.wireOp",EDGE,"E0");var subQ2=makeQuery(id+"F0.imprint","INTERSECT",VERTEX,{"disambiguationData":[OD(1.0)],"derivedFrom":[subQ1,subQ0]});Q65=makeQuery(id+"F0.imprint","IMPRINT",FACE,{"disambiguationData":[TD([[makeQuery(id+"F0.imprint","IMPRINT",EDGE,{"disambiguationData":[TD([[subQ2,-1.0]])],"derivedFrom":subQ1}),1.0]])]});}
            var Q66;
            {var subQ0=sQuery(id+"F0.wireOp",EDGE,"E13");var subQ1=sQuery(id+"F0.wireOp",EDGE,"E9.3");var subQ2=makeQuery(id+"F0.imprint","INTERSECT",VERTEX,{"derivedFrom":[subQ1,subQ0]});Q66=makeQuery(id+"F0.imprint","IMPRINT",FACE,{"disambiguationData":[TD([[makeQuery(id+"F0.imprint","IMPRINT",EDGE,{"disambiguationData":[TD([[subQ2,-1.0]])],"derivedFrom":subQ1}),-1.0]])]});}
            var Q67;
            {var subQ0=sQuery(id+"F0.wireOp",EDGE,"E28");var subQ1=sQuery(id+"F0.wireOp",EDGE,"E13");var subQ2=makeQuery(id+"F0.imprint","INTERSECT",VERTEX,{"disambiguationData":[OD(0.0)],"derivedFrom":[subQ1,subQ0]});Q67=makeQuery(id+"F0.imprint","IMPRINT",FACE,{"disambiguationData":[TD([[makeQuery(id+"F0.imprint","IMPRINT",EDGE,{"disambiguationData":[TD([[subQ2,1.0]])],"derivedFrom":subQ1}),1.0]])]});}
            var Q68;
            {var subQ0=sQuery(id+"F0.wireOp",EDGE,"E14");var subQ1=sQuery(id+"F0.wireOp",EDGE,"E9.4");var subQ2=makeQuery(id+"F0.imprint","INTERSECT",VERTEX,{"derivedFrom":[subQ1,subQ0]});Q68=makeQuery(id+"F0.imprint","IMPRINT",FACE,{"disambiguationData":[TD([[makeQuery(id+"F0.imprint","IMPRINT",EDGE,{"disambiguationData":[TD([[subQ2,-1.0]])],"derivedFrom":subQ1}),-1.0]])]});}
            var Q69;
            {var subQ0=sQuery(id+"F0.wireOp",EDGE,"E13");var subQ1=sQuery(id+"F0.wireOp",EDGE,"E0");var subQ2=makeQuery(id+"F0.imprint","INTERSECT",VERTEX,{"disambiguationData":[OD(0.0)],"derivedFrom":[subQ1,subQ0]});Q69=makeQuery(id+"F0.imprint","IMPRINT",FACE,{"disambiguationData":[TD([[makeQuery(id+"F0.imprint","IMPRINT",EDGE,{"disambiguationData":[TD([[subQ2,-1.0]])],"derivedFrom":subQ1}),1.0]])]});}
            var Q70;
            {var subQ1=sQuery(id+"F0.wireOp",EDGE,"E5");var subQ7=sQuery(id+"F0.wireOp",EDGE,"E4");var subQ9=makeQuery(id+"F0.imprint","INTERSECT",VERTEX,{"derivedFrom":[subQ7,subQ1]});Q70=makeQuery(id+"F0.imprint","IMPRINT",FACE,{"disambiguationData":[TD([[makeQuery(id+"F0.imprint","IMPRINT",EDGE,{"disambiguationData":[TD([[subQ9,-1.0]])],"derivedFrom":subQ7}),1.0]])]});}
            var Q71;
            {var subQ0=sQuery(id+"F0.wireOp",EDGE,"E28");var subQ1=sQuery(id+"F0.wireOp",EDGE,"E10");var subQ5=makeQuery(id+"F0.imprint","INTERSECT",VERTEX,{"disambiguationData":[OD(0.0)],"derivedFrom":[subQ1,subQ0]});Q71=makeQuery(id+"F0.imprint","IMPRINT",FACE,{"disambiguationData":[TD([[makeQuery(id+"F0.imprint","IMPRINT",EDGE,{"disambiguationData":[TD([[subQ5,-1.0]])],"derivedFrom":subQ1}),-1.0]])]});}
            var Q72;
            {var subQ1=sQuery(id+"F0.wireOp",EDGE,"E4");var subQ5=sQuery(id+"F0.wireOp",EDGE,"E5");var subQ6=makeQuery(id+"F0.imprint","INTERSECT",VERTEX,{"derivedFrom":[subQ1,subQ5]});Q72=makeQuery(id+"F0.imprint","IMPRINT",FACE,{"disambiguationData":[TD([[makeQuery(id+"F0.imprint","IMPRINT",EDGE,{"disambiguationData":[TD([[subQ6,-1.0]])],"derivedFrom":subQ1}),-1.0]])]});}
            var Q73;
            {var subQ0=sQuery(id+"F0.wireOp",EDGE,"E18");var subQ1=sQuery(id+"F0.wireOp",EDGE,"E4");var subQ2=makeQuery(id+"F0.imprint","INTERSECT",VERTEX,{"derivedFrom":[subQ1,subQ0]});Q73=makeQuery(id+"F0.imprint","IMPRINT",FACE,{"disambiguationData":[TD([[makeQuery(id+"F0.imprint","IMPRINT",EDGE,{"disambiguationData":[TD([[subQ2,-1.0]])],"derivedFrom":subQ1}),-1.0]])]});}
            var Q74;
            {var subQ0=sQuery(id+"F0.wireOp",EDGE,"E20");var subQ1=sQuery(id+"F0.wireOp",EDGE,"E6");var subQ2=makeQuery(id+"F0.imprint","INTERSECT",VERTEX,{"derivedFrom":[subQ1,subQ0]});Q74=makeQuery(id+"F0.imprint","IMPRINT",FACE,{"disambiguationData":[TD([[makeQuery(id+"F0.imprint","IMPRINT",EDGE,{"disambiguationData":[TD([[subQ2,-1.0]])],"derivedFrom":subQ1}),-1.0]])]});}
            var Q75;
            {var subQ0=sQuery(id+"F0.wireOp",EDGE,"E6");var subQ1=sQuery(id+"F0.wireOp",EDGE,"E4");var subQ2=makeQuery(id+"F0.imprint","INTERSECT",VERTEX,{"disambiguationData":[OD(1.0)],"derivedFrom":[subQ1,subQ0]});Q75=makeQuery(id+"F0.imprint","IMPRINT",FACE,{"disambiguationData":[TD([[makeQuery(id+"F0.imprint","IMPRINT",EDGE,{"disambiguationData":[TD([[subQ2,1.0]])],"derivedFrom":subQ0}),-1.0]])]});}
            var Q76;
            {var subQ0=sQuery(id+"F0.wireOp",EDGE,"E6");var subQ1=sQuery(id+"F0.wireOp",EDGE,"E4");var subQ2=makeQuery(id+"F0.imprint","INTERSECT",VERTEX,{"disambiguationData":[OD(1.0)],"derivedFrom":[subQ1,subQ0]});Q76=makeQuery(id+"F0.imprint","IMPRINT",FACE,{"disambiguationData":[TD([[makeQuery(id+"F0.imprint","IMPRINT",EDGE,{"disambiguationData":[TD([[subQ2,-1.0]])],"derivedFrom":subQ0}),-1.0]])]});}
            var Q77;
            {var subQ0=sQuery(id+"F0.wireOp",EDGE,"E19");var subQ1=sQuery(id+"F0.wireOp",EDGE,"E6");var subQ2=makeQuery(id+"F0.imprint","INTERSECT",VERTEX,{"derivedFrom":[subQ1,subQ0]});Q77=makeQuery(id+"F0.imprint","IMPRINT",FACE,{"disambiguationData":[TD([[makeQuery(id+"F0.imprint","IMPRINT",EDGE,{"disambiguationData":[TD([[subQ2,1.0]])],"derivedFrom":subQ1}),-1.0]])]});}
            var Q78;
            {var subQ0=sQuery(id+"F0.wireOp",EDGE,"E28");var subQ1=sQuery(id+"F0.wireOp",EDGE,"E11");var subQ9=makeQuery(id+"F0.imprint","INTERSECT",VERTEX,{"disambiguationData":[OD(0.0)],"derivedFrom":[subQ1,subQ0]});Q78=makeQuery(id+"F0.imprint","IMPRINT",FACE,{"disambiguationData":[TD([[makeQuery(id+"F0.imprint","IMPRINT",EDGE,{"disambiguationData":[TD([[subQ9,-1.0]])],"derivedFrom":subQ1}),-1.0]])]});}
            var Q79;
            {var subQ0=sQuery(id+"F0.wireOp",EDGE,"E28");var subQ1=sQuery(id+"F0.wireOp",EDGE,"E12");var subQ2=makeQuery(id+"F0.imprint","INTERSECT",VERTEX,{"disambiguationData":[OD(0.0)],"derivedFrom":[subQ1,subQ0]});Q79=makeQuery(id+"F0.imprint","IMPRINT",FACE,{"disambiguationData":[TD([[makeQuery(id+"F0.imprint","IMPRINT",EDGE,{"disambiguationData":[TD([[subQ2,-1.0]])],"derivedFrom":subQ1}),-1.0]])]});}
            var Q80;
            {var subQ0=sQuery(id+"F0.wireOp",EDGE,"E28");var subQ1=sQuery(id+"F0.wireOp",EDGE,"E13");var subQ2=makeQuery(id+"F0.imprint","INTERSECT",VERTEX,{"disambiguationData":[OD(0.0)],"derivedFrom":[subQ1,subQ0]});Q80=makeQuery(id+"F0.imprint","IMPRINT",FACE,{"disambiguationData":[TD([[makeQuery(id+"F0.imprint","IMPRINT",EDGE,{"disambiguationData":[TD([[subQ2,1.0]])],"derivedFrom":subQ1}),-1.0]])]});}
            var Q81;
            {var subQ0=sQuery(id+"F0.wireOp",EDGE,"E18");var subQ1=sQuery(id+"F0.wireOp",EDGE,"E4");var subQ2=makeQuery(id+"F0.imprint","INTERSECT",VERTEX,{"derivedFrom":[subQ1,subQ0]});Q81=makeQuery(id+"F0.imprint","IMPRINT",FACE,{"disambiguationData":[TD([[makeQuery(id+"F0.imprint","IMPRINT",EDGE,{"disambiguationData":[TD([[subQ2,-1.0]])],"derivedFrom":subQ1}),1.0]])]});}
            var Q82;
            {var subQ0=sQuery(id+"F0.wireOp",EDGE,"E31");var subQ1=sQuery(id+"F0.wireOp",EDGE,"E13");var subQ2=makeQuery(id+"F0.imprint","INTERSECT",VERTEX,{"disambiguationData":[OD(1.0)],"derivedFrom":[subQ1,subQ0]});Q82=makeQuery(id+"F0.imprint","IMPRINT",FACE,{"disambiguationData":[TD([[makeQuery(id+"F0.imprint","IMPRINT",EDGE,{"disambiguationData":[TD([[subQ2,-1.0]])],"derivedFrom":subQ1}),-1.0]])]});}
            var Q83;
            {var subQ0=sQuery(id+"F0.wireOp",EDGE,"E28");var subQ1=sQuery(id+"F0.wireOp",EDGE,"E12");var subQ2=makeQuery(id+"F0.imprint","INTERSECT",VERTEX,{"disambiguationData":[OD(1.0)],"derivedFrom":[subQ1,subQ0]});Q83=makeQuery(id+"F0.imprint","IMPRINT",FACE,{"disambiguationData":[TD([[makeQuery(id+"F0.imprint","IMPRINT",EDGE,{"disambiguationData":[TD([[subQ2,-1.0]])],"derivedFrom":subQ1}),-1.0]])]});}
            var Q84;
            {var subQ0=sQuery(id+"F0.wireOp",EDGE,"E32");var subQ1=sQuery(id+"F0.wireOp",EDGE,"E12");var subQ2=makeQuery(id+"F0.imprint","INTERSECT",VERTEX,{"disambiguationData":[OD(1.0)],"derivedFrom":[subQ1,subQ0]});Q84=makeQuery(id+"F0.imprint","IMPRINT",FACE,{"disambiguationData":[TD([[makeQuery(id+"F0.imprint","IMPRINT",EDGE,{"disambiguationData":[TD([[subQ2,-1.0]])],"derivedFrom":subQ1}),-1.0]])]});}
            var Q85;
            {var subQ0=sQuery(id+"F0.wireOp",EDGE,"E28");var subQ1=sQuery(id+"F0.wireOp",EDGE,"E11");var subQ2=makeQuery(id+"F0.imprint","INTERSECT",VERTEX,{"disambiguationData":[OD(1.0)],"derivedFrom":[subQ1,subQ0]});Q85=makeQuery(id+"F0.imprint","IMPRINT",FACE,{"disambiguationData":[TD([[makeQuery(id+"F0.imprint","IMPRINT",EDGE,{"disambiguationData":[TD([[subQ2,-1.0]])],"derivedFrom":subQ1}),-1.0]])]});}
            var Q86;
            {var subQ0=sQuery(id+"F0.wireOp",EDGE,"E33");var subQ1=sQuery(id+"F0.wireOp",EDGE,"E11");var subQ2=makeQuery(id+"F0.imprint","INTERSECT",VERTEX,{"disambiguationData":[OD(1.0)],"derivedFrom":[subQ1,subQ0]});Q86=makeQuery(id+"F0.imprint","IMPRINT",FACE,{"disambiguationData":[TD([[makeQuery(id+"F0.imprint","IMPRINT",EDGE,{"disambiguationData":[TD([[subQ2,-1.0]])],"derivedFrom":subQ1}),-1.0]])]});}
            var Q87;
            {var subQ0=sQuery(id+"F0.wireOp",EDGE,"E28");var subQ1=sQuery(id+"F0.wireOp",EDGE,"E10");var subQ2=makeQuery(id+"F0.imprint","INTERSECT",VERTEX,{"disambiguationData":[OD(1.0)],"derivedFrom":[subQ1,subQ0]});Q87=makeQuery(id+"F0.imprint","IMPRINT",FACE,{"disambiguationData":[TD([[makeQuery(id+"F0.imprint","IMPRINT",EDGE,{"disambiguationData":[TD([[subQ2,-1.0]])],"derivedFrom":subQ1}),-1.0]])]});}
            var Q88;
            {var subQ0=sQuery(id+"F0.wireOp",EDGE,"E29");var subQ1=sQuery(id+"F0.wireOp",EDGE,"E10");var subQ2=makeQuery(id+"F0.imprint","INTERSECT",VERTEX,{"disambiguationData":[OD(1.0)],"derivedFrom":[subQ1,subQ0]});Q88=makeQuery(id+"F0.imprint","IMPRINT",FACE,{"disambiguationData":[TD([[makeQuery(id+"F0.imprint","IMPRINT",EDGE,{"disambiguationData":[TD([[subQ2,-1.0]])],"derivedFrom":subQ1}),-1.0]])]});}
            var Q89;
            {var subQ0=sQuery(id+"F0.wireOp",EDGE,"E28");var subQ1=sQuery(id+"F0.wireOp",EDGE,"E5");var subQ2=makeQuery(id+"F0.imprint","INTERSECT",VERTEX,{"disambiguationData":[OD(1.0)],"derivedFrom":[subQ1,subQ0]});Q89=makeQuery(id+"F0.imprint","IMPRINT",FACE,{"disambiguationData":[TD([[makeQuery(id+"F0.imprint","IMPRINT",EDGE,{"disambiguationData":[TD([[subQ2,-1.0]])],"derivedFrom":subQ1}),-1.0]])]});}
            var Q90;
            {var subQ0=sQuery(id+"F0.wireOp",EDGE,"E30");var subQ1=sQuery(id+"F0.wireOp",EDGE,"E5");var subQ2=makeQuery(id+"F0.imprint","INTERSECT",VERTEX,{"disambiguationData":[OD(1.0)],"derivedFrom":[subQ1,subQ0]});Q90=makeQuery(id+"F0.imprint","IMPRINT",FACE,{"disambiguationData":[TD([[makeQuery(id+"F0.imprint","IMPRINT",EDGE,{"disambiguationData":[TD([[subQ2,-1.0]])],"derivedFrom":subQ1}),-1.0]])]});}
            var Q91;
            {var subQ0=sQuery(id+"F0.wireOp",EDGE,"E30");var subQ1=sQuery(id+"F0.wireOp",EDGE,"E13");var subQ2=makeQuery(id+"F0.imprint","INTERSECT",VERTEX,{"disambiguationData":[OD(0.0)],"derivedFrom":[subQ1,subQ0]});Q91=makeQuery(id+"F0.imprint","IMPRINT",FACE,{"disambiguationData":[TD([[makeQuery(id+"F0.imprint","IMPRINT",EDGE,{"disambiguationData":[TD([[subQ2,1.0]])],"derivedFrom":subQ1}),-1.0]])]});}
            var Q92;
            Q92=sQuery(id+"F0.wireOp",EDGE,"E5");
            var Q93;
            Q93=sQuery(id+"F0.wireOp",EDGE,"E2.2");
            var Q94;
            Q94=sQuery(id+"F0.wireOp",EDGE,"E2.0");
            var Q95;
            Q95=sQuery(id+"F0.wireOp",EDGE,"dxAisywA-VBGr-Pawd-wR7n-FkVNZc5FjTRd");
            var Q96;
            Q96=sQuery(id+"F0.wireOp",EDGE,"E2.1");
            var Q97;
            Q97=sQuery(id+"F0.wireOp",EDGE,"RqG3pEgj-UPx2-bqY4-tycd-a4pZXK4rwrWL");
            extrude(context, id + "F1", {"entities" : qUnion([Q0, Q1, Q2, Q3, Q4, Q5, Q6, Q7, Q8, Q9, Q10, Q11, Q12, Q13, Q14, Q15, Q16, Q17, Q18, Q19, Q20, Q21, Q22, Q23, Q24, Q25, Q26, Q27, Q28, Q29, Q30, Q31, Q32, Q33, Q34, Q35, Q36, Q37, Q38, Q39, Q40, Q41, Q42, Q43, Q44, Q45, Q46, Q47, Q48, Q49, Q50, Q51, Q52, Q53, Q54, Q55, Q56, Q57, Q58, Q59, Q60, Q61, Q62, Q63, Q64, Q65, Q66, Q67, Q68, Q69, Q70, Q71, Q72, Q73, Q74, Q75, Q76, Q77, Q78, Q79, Q80, Q81, Q82, Q83, Q84, Q85, Q86, Q87, Q88, Q89, Q90, Q91]), "surfaceEntities" : qUnion([Q92, Q93, Q94, Q95, Q96, Q97]), "endBound" : BoundingType.SYMMETRIC, "oppositeDirection" : true, "depth" : 7 * mm, "offsetDistance" : 25 * mm});
        }
        {
            var Q0;
            Q0=makeQuery(id+"F1.opExtrude","CAP_EDGE",EDGE,{"disambiguationData":[OSD([sQuery(id+"F0.wireOp",EDGE,"E11")])],"isStart":true});
            var Q1;
            Q1=makeQuery(id+"F1.opExtrude","CAP_EDGE",EDGE,{"disambiguationData":[OSD([sQuery(id+"F0.wireOp",EDGE,"E33")])],"isStart":true});
            var Q2;
            Q2=makeQuery(id+"F1.opExtrude","CAP_EDGE",EDGE,{"disambiguationData":[OSD([sQuery(id+"F0.wireOp",EDGE,"E10")])],"isStart":true});
            var Q3;
            Q3=makeQuery(id+"F1.opExtrude","CAP_EDGE",EDGE,{"disambiguationData":[OSD([sQuery(id+"F0.wireOp",EDGE,"E29")])],"isStart":true});
            var Q4;
            Q4=makeQuery(id+"F1.opExtrude","CAP_EDGE",EDGE,{"disambiguationData":[OSD([sQuery(id+"F0.wireOp",EDGE,"E5")])],"isStart":true});
            var Q5;
            Q5=makeQuery(id+"F1.opExtrude","CAP_EDGE",EDGE,{"disambiguationData":[OSD([sQuery(id+"F0.wireOp",EDGE,"E30")])],"isStart":true});
            var Q6;
            Q6=makeQuery(id+"F1.opExtrude","CAP_EDGE",EDGE,{"disambiguationData":[OSD([sQuery(id+"F0.wireOp",EDGE,"E31")])],"isStart":true});
            var Q7;
            Q7=makeQuery(id+"F1.opExtrude","CAP_EDGE",EDGE,{"disambiguationData":[OSD([sQuery(id+"F0.wireOp",EDGE,"E12")])],"isStart":true});
            var Q8;
            Q8=makeQuery(id+"F1.opExtrude","CAP_EDGE",EDGE,{"disambiguationData":[OSD([sQuery(id+"F0.wireOp",EDGE,"E32")])],"isStart":true});
            var Q9;
            Q9=makeQuery(id+"F1.opExtrude","CAP_EDGE",EDGE,{"disambiguationData":[OSD([sQuery(id+"F0.wireOp",EDGE,"E13")])],"isStart":true});
            fillet(context, id + "F2", {"entities" : qUnion([Q0, Q1, Q2, Q3, Q4, Q5, Q6, Q7, Q8, Q9]), "radius" : 2 * mm, "tangentPropagation" : true, "allowEdgeOverflow" : false});
        }
        {
            var Q0;
            Q0=makeQuery(id+"F1.opExtrude","CAP_EDGE",EDGE,{"disambiguationData":[OSD([sQuery(id+"F0.wireOp",EDGE,"E5")])],"isStart":false});
            var Q1;
            Q1=makeQuery(id+"F1.opExtrude","CAP_EDGE",EDGE,{"disambiguationData":[OSD([sQuery(id+"F0.wireOp",EDGE,"E30")])],"isStart":false});
            var Q2;
            Q2=makeQuery(id+"F1.opExtrude","CAP_EDGE",EDGE,{"disambiguationData":[OSD([sQuery(id+"F0.wireOp",EDGE,"E13")])],"isStart":false});
            var Q3;
            Q3=makeQuery(id+"F1.opExtrude","CAP_EDGE",EDGE,{"disambiguationData":[OSD([sQuery(id+"F0.wireOp",EDGE,"E31")])],"isStart":false});
            var Q4;
            Q4=makeQuery(id+"F1.opExtrude","CAP_EDGE",EDGE,{"disambiguationData":[OSD([sQuery(id+"F0.wireOp",EDGE,"E12")])],"isStart":false});
            var Q5;
            Q5=makeQuery(id+"F1.opExtrude","CAP_EDGE",EDGE,{"disambiguationData":[OSD([sQuery(id+"F0.wireOp",EDGE,"E32")])],"isStart":false});
            var Q6;
            Q6=makeQuery(id+"F1.opExtrude","CAP_EDGE",EDGE,{"disambiguationData":[OSD([sQuery(id+"F0.wireOp",EDGE,"E11")])],"isStart":false});
            var Q7;
            Q7=makeQuery(id+"F1.opExtrude","CAP_EDGE",EDGE,{"disambiguationData":[OSD([sQuery(id+"F0.wireOp",EDGE,"E33")])],"isStart":false});
            var Q8;
            Q8=makeQuery(id+"F1.opExtrude","CAP_EDGE",EDGE,{"disambiguationData":[OSD([sQuery(id+"F0.wireOp",EDGE,"E10")])],"isStart":false});
            var Q9;
            Q9=makeQuery(id+"F1.opExtrude","CAP_EDGE",EDGE,{"disambiguationData":[OSD([sQuery(id+"F0.wireOp",EDGE,"E29")])],"isStart":false});
            fillet(context, id + "F3", {"entities" : qUnion([Q0, Q1, Q2, Q3, Q4, Q5, Q6, Q7, Q8, Q9]), "radius" : 2 * mm, "tangentPropagation" : true, "allowEdgeOverflow" : false});
        }
    });
